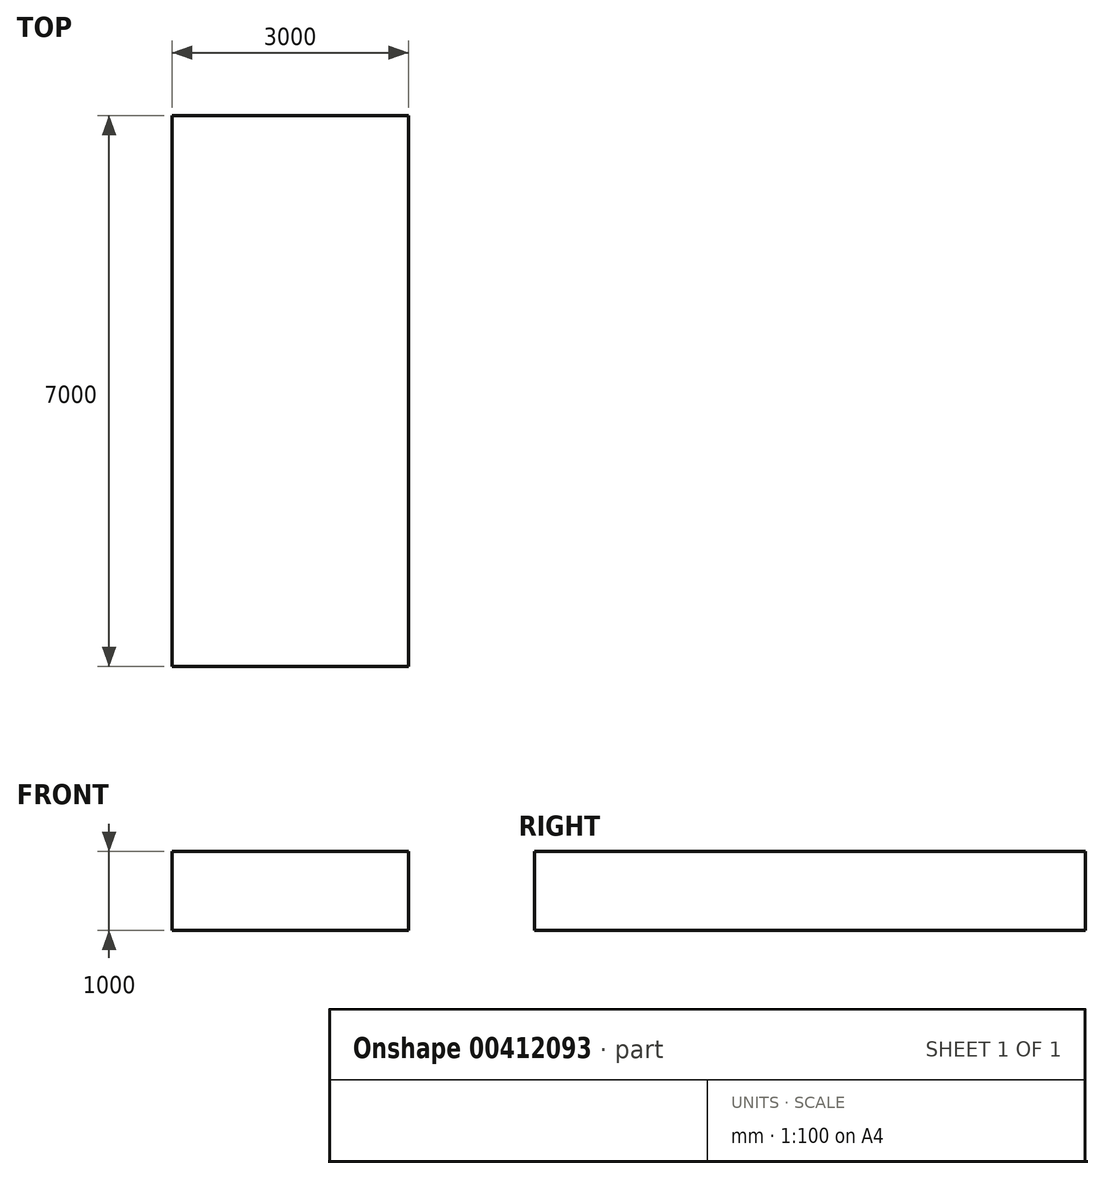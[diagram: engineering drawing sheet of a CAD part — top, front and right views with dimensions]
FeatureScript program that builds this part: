
annotation { "Feature Type Name" : "Feature", "Feature Type Description" : "" }
export const myFeature = defineFeature(function(context is Context, id is Id, definition is map)
    precondition{}
    {
        {
            var Q0;
            Q0=qCreatedBy(makeId("Front.planeOp"),FACE);
            var sketch = newSketch(context, id + "F0", { "sketchPlane" : qUnion([Q0])});
            skLineSegment(sketch, "E0.bottom", {"start": v(-1491.43, -48.37) * mm, "end": v(1508.57, -48.37) * mm});
            skLineSegment(sketch, "E0.top", {"start": v(-1491.43, -1048.37) * mm, "end": v(1508.57, -1048.37) * mm});
            skLineSegment(sketch, "E0.left", {"start": v(-1491.43, -48.37) * mm, "end": v(-1491.43, -1048.37) * mm});
            skLineSegment(sketch, "E0.right", {"start": v(1508.57, -48.37) * mm, "end": v(1508.57, -1048.37) * mm});
            skSolve(sketch);
        }
        {
            var Q0;
            Q0 = qSketchRegion(id + "F0", true);
            extrude(context, id + "F1", {"entities" : qUnion([Q0]), "depth" : 7000 * mm});
        }
    });
